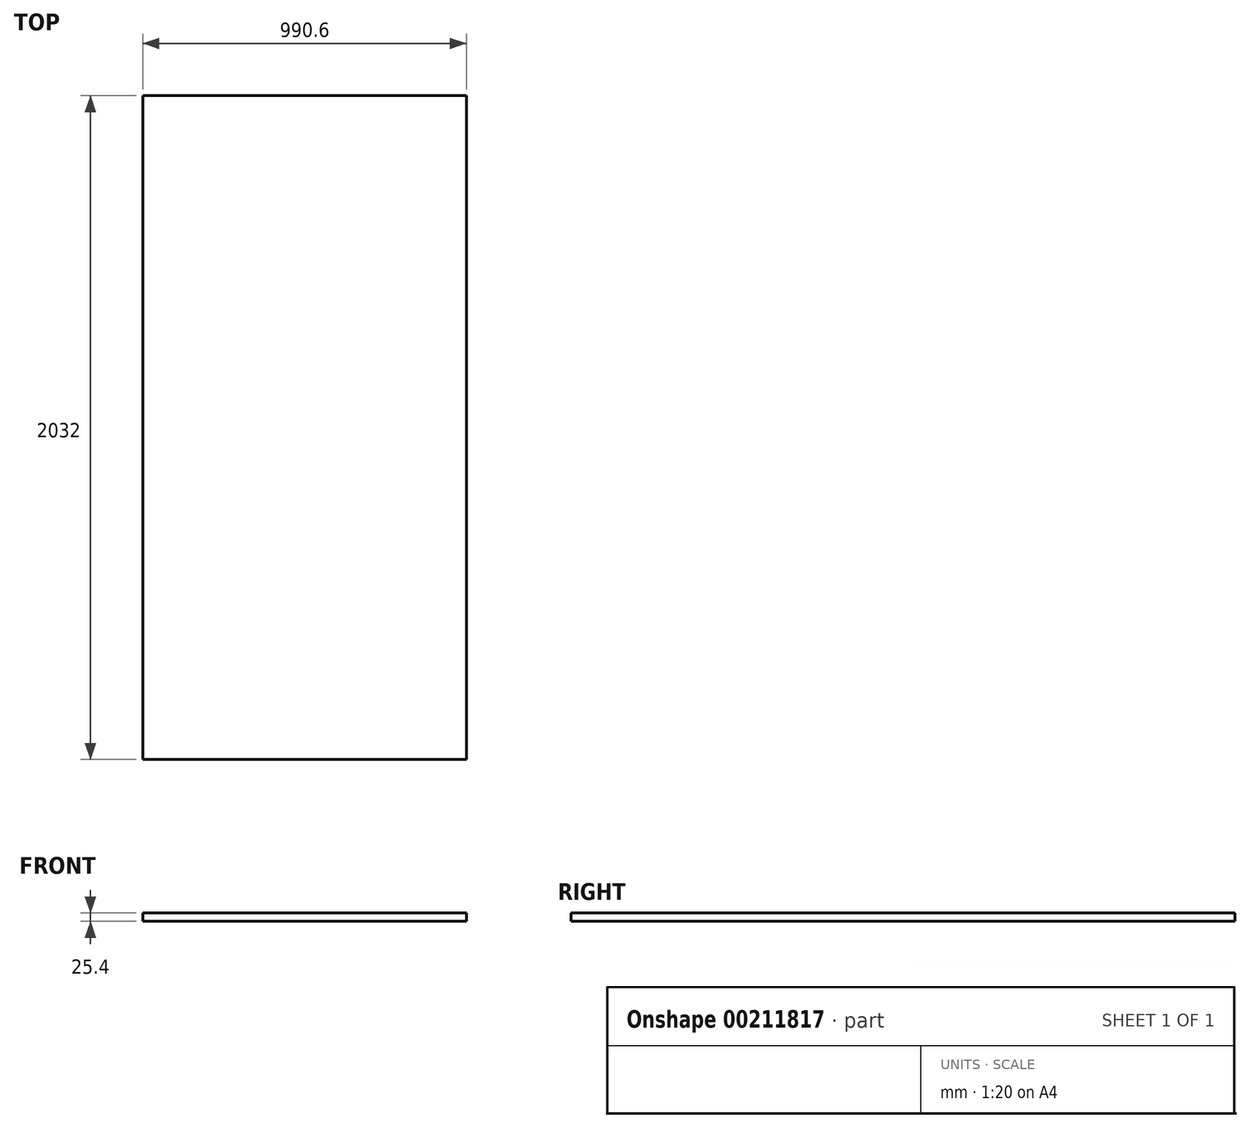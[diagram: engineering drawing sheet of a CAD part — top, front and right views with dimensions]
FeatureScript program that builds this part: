
annotation { "Feature Type Name" : "Feature", "Feature Type Description" : "" }
export const myFeature = defineFeature(function(context is Context, id is Id, definition is map)
    precondition{}
    {
        {
            var Q0;
            Q0=qCreatedBy(makeId("Top.planeOp"),FACE);
            var sketch = newSketch(context, id + "F0", { "sketchPlane" : qUnion([Q0])});
            skLineSegment(sketch, "E0.bottom", {"start": v(0, 0) * mm, "end": v(990.6, 0) * mm});
            skLineSegment(sketch, "E0.top", {"start": v(0, 2032) * mm, "end": v(990.6, 2032) * mm});
            skLineSegment(sketch, "E0.left", {"start": v(0, 0) * mm, "end": v(0, 2032) * mm});
            skLineSegment(sketch, "E0.right", {"start": v(990.6, 0) * mm, "end": v(990.6, 2032) * mm});
            skSolve(sketch);
        }
        {
            var Q0;
            Q0 = qSketchRegion(id + "F0", true);
            extrude(context, id + "F1", {"entities" : qUnion([Q0]), "depth" : 25.4 * mm});
        }
    });
